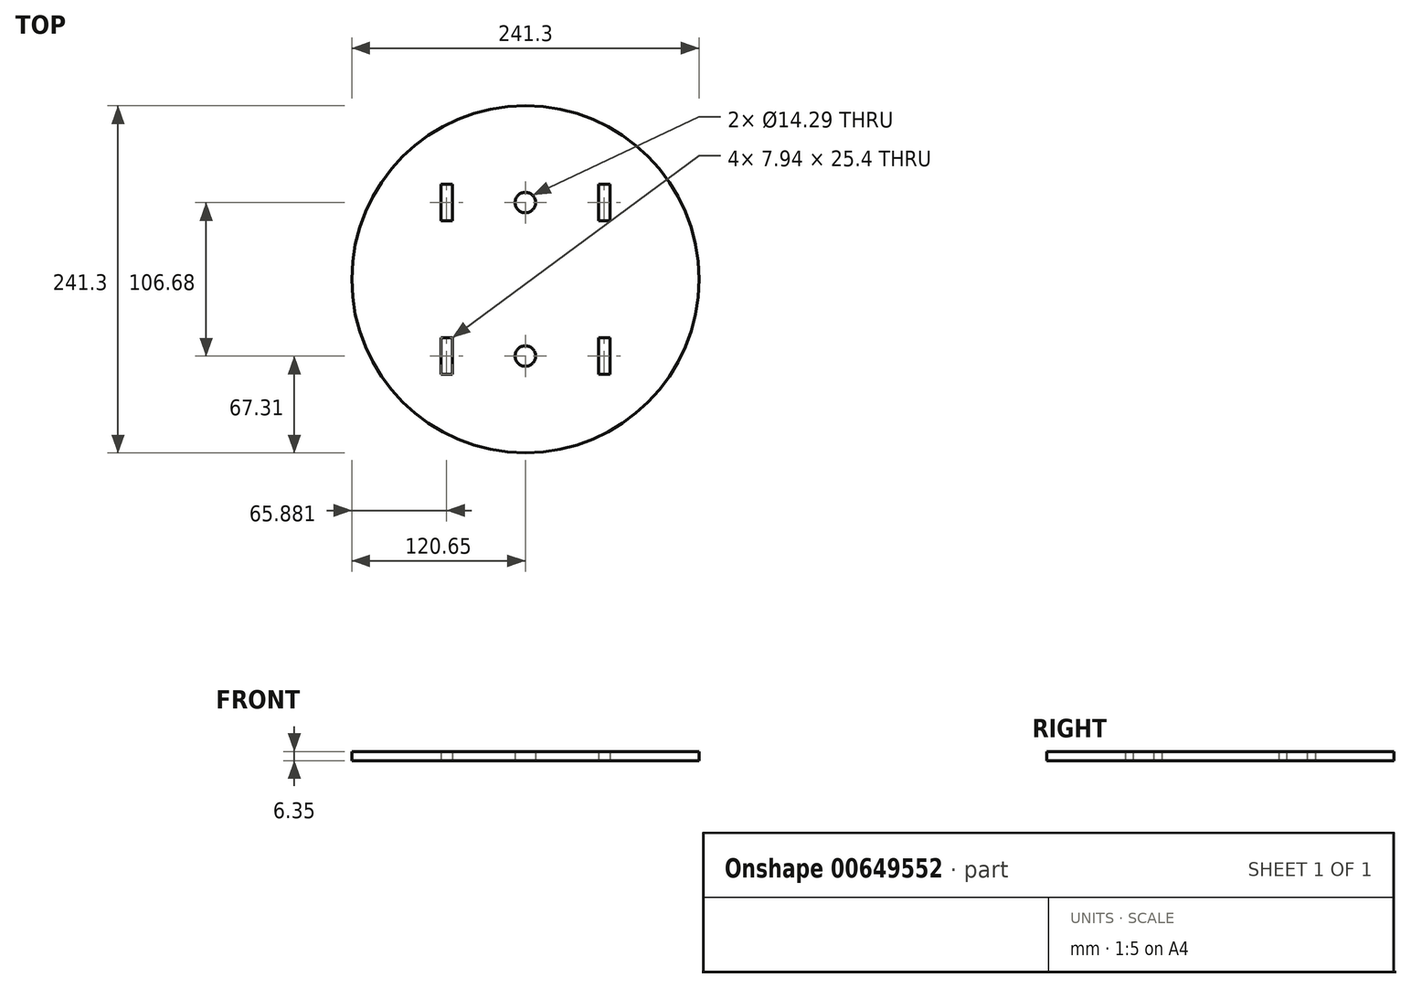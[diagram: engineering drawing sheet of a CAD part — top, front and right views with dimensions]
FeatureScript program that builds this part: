
annotation { "Feature Type Name" : "Feature", "Feature Type Description" : "" }
export const myFeature = defineFeature(function(context is Context, id is Id, definition is map)
    precondition{}
    {
        {
            var Q0;
            Q0=qCreatedBy(makeId("Top.planeOp"), FACE);
            var sketch = newSketch(context, id + "F0", { "sketchPlane" : qUnion([Q0])});
            skCircle(sketch, "E0", {"center": v(0, 0) * mm, "radius": 120.65 * mm});
            skCircle(sketch, "E1", {"center": v(0, 53.34) * mm, "radius": 7.14 * mm});
            skCircle(sketch, "E2", {"center": v(0, -53.34) * mm, "radius": 7.14 * mm});
            skLineSegment(sketch, "E3.bottom", {"start": v(50.8, 66.04) * mm, "end": v(58.74, 66.04) * mm});
            skLineSegment(sketch, "E3.top", {"start": v(50.8, 40.64) * mm, "end": v(58.74, 40.64) * mm});
            skLineSegment(sketch, "E3.left", {"start": v(50.8, 66.04) * mm, "end": v(50.8, 40.64) * mm});
            skLineSegment(sketch, "E3.right", {"start": v(58.74, 66.04) * mm, "end": v(58.74, 40.64) * mm});
            skLineSegment(sketch, "E4.bottom", {"start": v(-58.74, 66.04) * mm, "end": v(-50.8, 66.04) * mm});
            skLineSegment(sketch, "E4.top", {"start": v(-58.74, 40.64) * mm, "end": v(-50.8, 40.64) * mm});
            skLineSegment(sketch, "E4.left", {"start": v(-58.74, 66.04) * mm, "end": v(-58.74, 40.64) * mm});
            skLineSegment(sketch, "E4.right", {"start": v(-50.8, 66.04) * mm, "end": v(-50.8, 40.64) * mm});
            skLineSegment(sketch, "E5.bottom", {"start": v(-50.8, -40.64) * mm, "end": v(-58.74, -40.64) * mm});
            skLineSegment(sketch, "E5.top", {"start": v(-50.8, -66.04) * mm, "end": v(-58.74, -66.04) * mm});
            skLineSegment(sketch, "E5.left", {"start": v(-50.8, -40.64) * mm, "end": v(-50.8, -66.04) * mm});
            skLineSegment(sketch, "E5.right", {"start": v(-58.74, -40.64) * mm, "end": v(-58.74, -66.04) * mm});
            skLineSegment(sketch, "E6.bottom", {"start": v(50.8, -40.64) * mm, "end": v(58.74, -40.64) * mm});
            skLineSegment(sketch, "E6.top", {"start": v(50.8, -66.04) * mm, "end": v(58.74, -66.04) * mm});
            skLineSegment(sketch, "E6.left", {"start": v(50.8, -40.64) * mm, "end": v(50.8, -66.04) * mm});
            skLineSegment(sketch, "E6.right", {"start": v(58.74, -40.64) * mm, "end": v(58.74, -66.04) * mm});
            skLineSegment(sketch, "E7", {"start": v(0, 53.34) * mm, "end": v(0, -53.34) * mm, "construction": true});
            skLineSegment(sketch, "E8", {"start": v(-50.8, -53.34) * mm, "end": v(50.8, -53.34) * mm, "construction": true});
            skLineSegment(sketch, "E9", {"start": v(50.8, 53.34) * mm, "end": v(-50.8, 53.34) * mm, "construction": true});
            skSolve(sketch);
        }
        {
            var Q0;
            Q0 = qSketchRegion(id + "F0", true);
            extrude(context, id + "F1", {"entities" : qUnion([Q0]), "depth" : 6.35 * mm, "offsetDistance" : 25.4 * mm});
        }
    });
